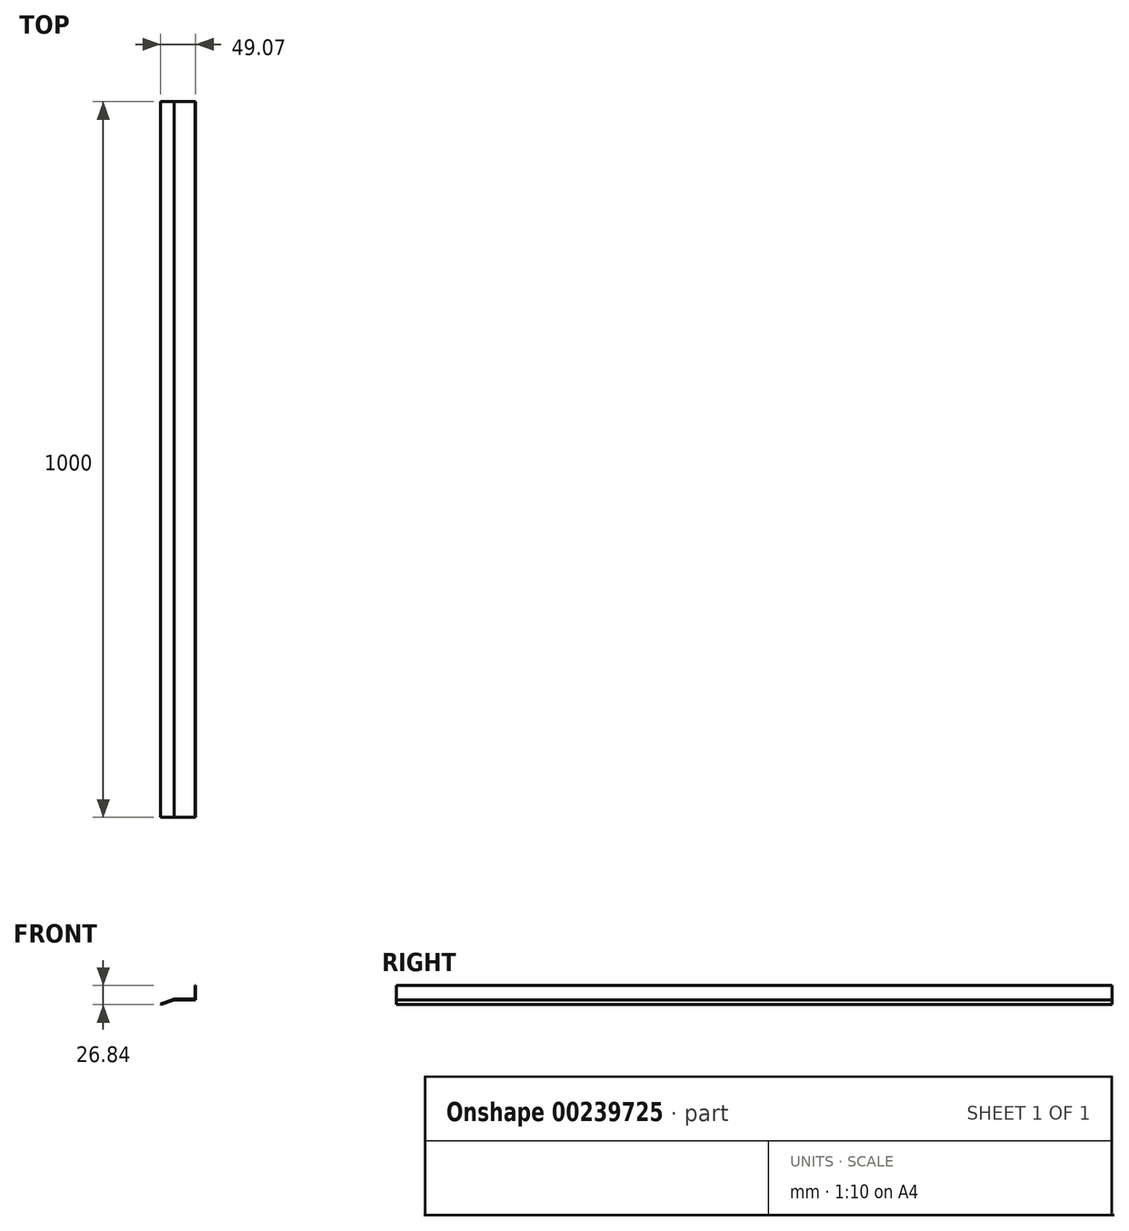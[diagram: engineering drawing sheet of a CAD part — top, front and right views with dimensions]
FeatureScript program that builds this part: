
annotation { "Feature Type Name" : "Feature", "Feature Type Description" : "" }
export const myFeature = defineFeature(function(context is Context, id is Id, definition is map)
    precondition{}
    {
        {
            var Q0;
            Q0=qCreatedBy(makeId("Front.planeOp"),FACE);
            var sketch = newSketch(context, id + "F0", { "sketchPlane" : qUnion([Q0])});
            skLineSegment(sketch, "E0", {"start": v(0, 0) * mm, "end": v(0, -20) * mm});
            skLineSegment(sketch, "E1", {"start": v(0, -20) * mm, "end": v(-30, -20) * mm});
            skLineSegment(sketch, "E2", {"start": v(-30, -20) * mm, "end": v(-48.8, -26.84) * mm});
            skLineSegment(sketch, "E3.0", {"start": v(-30.14, -19.2) * mm, "end": v(-49.07, -26.09) * mm});
            skLineSegment(sketch, "E3.1", {"start": v(-0.8, -19.2) * mm, "end": v(-30.14, -19.2) * mm});
            skLineSegment(sketch, "E3.2", {"start": v(-0.8, 0) * mm, "end": v(-0.8, -19.2) * mm});
            skLineSegment(sketch, "E4", {"start": v(-49.07, -26.09) * mm, "end": v(-48.8, -26.84) * mm});
            skLineSegment(sketch, "E5", {"start": v(0, 0) * mm, "end": v(-0.8, 0) * mm});
            skSolve(sketch);
        }
        {
            var Q0;
            Q0=makeQuery(id+"F0.imprint","IMPRINT",FACE,{"disambiguationData":[TD([[makeQuery(id+"F0.imprint","IMPRINT",EDGE,{"derivedFrom":sQuery(id+"F0.wireOp",EDGE,"E0")}),-1.0]])]});
            extrude(context, id + "F1", {"entities" : qUnion([Q0]), "depth" : 1000 * mm});
        }
    });
